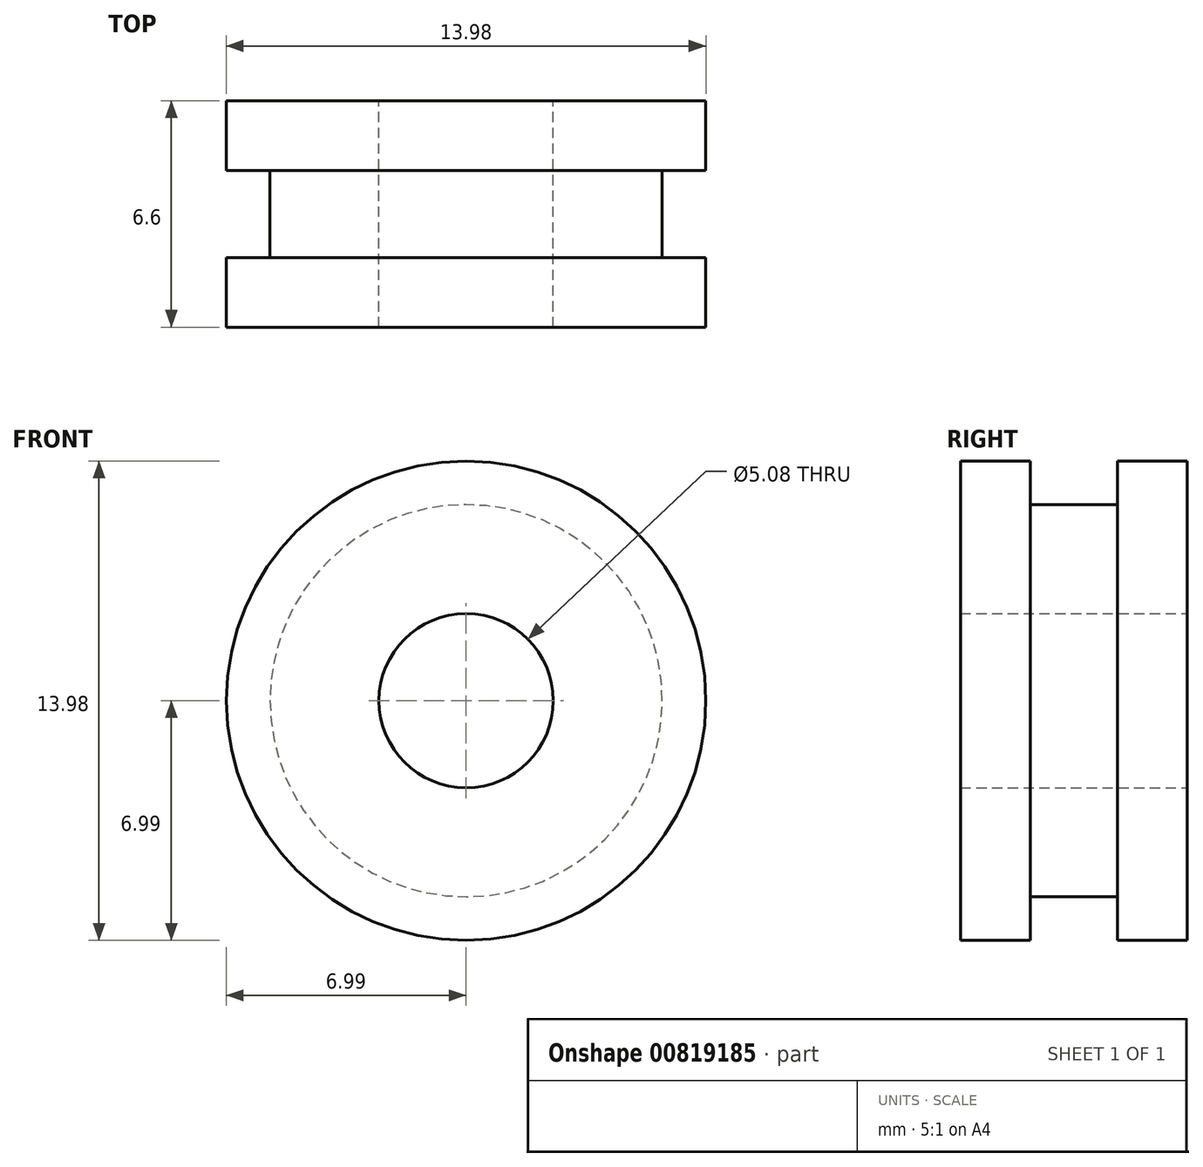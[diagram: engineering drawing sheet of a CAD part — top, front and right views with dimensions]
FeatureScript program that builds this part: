
annotation { "Feature Type Name" : "Feature", "Feature Type Description" : "" }
export const myFeature = defineFeature(function(context is Context, id is Id, definition is map)
    precondition{}
    {
        {
            var Q0;
            Q0=qCreatedBy(makeId("Front.planeOp"),FACE);
            var sketch = newSketch(context, id + "F0", { "sketchPlane" : qUnion([Q0])});
            skCircle(sketch, "E0", {"center": v(0, 0) * mm, "radius": 6.99 * mm});
            skSolve(sketch);
        }
        {
            var Q0;
            Q0 = qSketchRegion(id + "F0", true);
            extrude(context, id + "F1", {"entities" : qUnion([Q0]), "depth" : 2.03 * mm, "offsetDistance" : 25.4 * mm});
        }
        {
            var Q0;
            Q0=makeQuery(id+"F1.opExtrude","CAP_FACE",FACE,{"disambiguationData":[OSD([sQuery(id+"F0.wireOp",EDGE,"E0")])],"isStart":false});
            var sketch = newSketch(context, id + "F2", { "sketchPlane" : qUnion([Q0])});
            skCircle(sketch, "E1", {"center": v(0, 0) * mm, "radius": 5.72 * mm});
            skSolve(sketch);
        }
        {
            var Q0;
            Q0 = qSketchRegion(id + "F2", true);
            extrude(context, id + "F3", {"entities" : qUnion([Q0]), "operationType" : NewBodyOperationType.ADD, "depth" : 2.54 * mm, "offsetDistance" : 25.4 * mm});
        }
        {
            var Q0;
            Q0=makeQuery(id+"F3.opExtrude","CAP_FACE",FACE,{"disambiguationData":[OSD([sQuery(id+"F2.wireOp",EDGE,"E1")])],"isStart":false});
            var sketch = newSketch(context, id + "F4", { "sketchPlane" : qUnion([Q0])});
            skCircle(sketch, "E2", {"center": v(0, 0) * mm, "radius": 6.99 * mm});
            skSolve(sketch);
        }
        {
            var Q0;
            Q0 = qSketchRegion(id + "F4", true);
            extrude(context, id + "F5", {"entities" : qUnion([Q0]), "operationType" : NewBodyOperationType.ADD, "depth" : 2.03 * mm, "offsetDistance" : 25.4 * mm});
        }
        {
            var Q0;
            Q0=makeQuery(id+"F5.opExtrude","CAP_FACE",FACE,{"disambiguationData":[OSD([sQuery(id+"F4.wireOp",EDGE,"E2")])],"isStart":false});
            var sketch = newSketch(context, id + "F6", { "sketchPlane" : qUnion([Q0])});
            skCircle(sketch, "E3", {"center": v(0, 0) * mm, "radius": 2.54 * mm});
            skSolve(sketch);
        }
        {
            var Q0;
            Q0 = qSketchRegion(id + "F6", true);
            extrude(context, id + "F7", {"entities" : qUnion([Q0]), "operationType" : NewBodyOperationType.REMOVE, "depth" : 25.4 * mm, "offsetDistance" : 25.4 * mm, "symmetric" : true});
        }
    });
